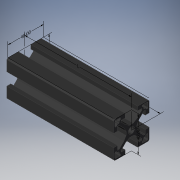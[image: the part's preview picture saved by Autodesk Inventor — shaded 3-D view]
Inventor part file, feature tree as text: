
AUTODESK INVENTOR PART (.ipt)
format: ipt  version: 2019 (Build 230136000, 136)  size: 272,896 bytes
history: native  units: mm
features: other x125, extrude x1, sketch x1
ambient origin geometry x8: Origin, YZ Plane, XZ Plane, XY Plane, X Axis, Y Axis, Z Axis, Center Point
bodies: Solid1 (feature_tree)
feature tree (127):
  other  "Annotations"
  extrude  "Extrusion1"  [1 undecoded]
  other  "CS_ANBAU_HINTEN_LINKS_XY"
  other  "CS_ANBAU_HINTEN_LINKS_YZ"
  other  "CS_ANBAU_HINTEN_LINKS_ZX"
  other  "CS_ANBAU_HINTEN_LINKS_X"
  other  "CS_ANBAU_HINTEN_LINKS_Y"
  other  "CS_ANBAU_HINTEN_LINKS_Z"
  other  "CS_ANBAU_HINTEN_LINKS_Center"
  other  "CS_ANBAU_HINTEN_OBEN_XY"
  other  "CS_ANBAU_HINTEN_OBEN_YZ"
  other  "CS_ANBAU_HINTEN_OBEN_ZX"
  other  "CS_ANBAU_HINTEN_OBEN_X"
  other  "CS_ANBAU_HINTEN_OBEN_Y"
  other  "CS_ANBAU_HINTEN_OBEN_Z"
  other  "CS_ANBAU_HINTEN_OBEN_Center"
  other  "CS_ANBAU_HINTEN_RECHTS_XY"
  other  "CS_ANBAU_HINTEN_RECHTS_YZ"
  other  "CS_ANBAU_HINTEN_RECHTS_ZX"
  other  "CS_ANBAU_HINTEN_RECHTS_X"
  other  "CS_ANBAU_HINTEN_RECHTS_Y"
  other  "CS_ANBAU_HINTEN_RECHTS_Z"
  other  "CS_ANBAU_HINTEN_RECHTS_Center"
  other  "CS_ANBAU_HINTEN_UNTEN_XY"
  other  "CS_ANBAU_HINTEN_UNTEN_YZ"
  other  "CS_ANBAU_HINTEN_UNTEN_ZX"
  other  "CS_ANBAU_HINTEN_UNTEN_X"
  other  "CS_ANBAU_HINTEN_UNTEN_Y"
  other  "CS_ANBAU_HINTEN_UNTEN_Z"
  other  "CS_ANBAU_HINTEN_UNTEN_Center"
  other  "CS_ANBAU_QUER_XY"
  other  "CS_ANBAU_QUER_YZ"
  other  "CS_ANBAU_QUER_ZX"
  other  "CS_ANBAU_QUER_X"
  other  "CS_ANBAU_QUER_Y"
  other  "CS_ANBAU_QUER_Z"
  other  "CS_ANBAU_QUER_Center"
  other  "CS_ANBAU_QUER_1_XY"
  other  "CS_ANBAU_QUER_1_YZ"
  other  "CS_ANBAU_QUER_1_ZX"
  other  "CS_ANBAU_QUER_1_X"
  other  "CS_ANBAU_QUER_1_Y"
  other  "CS_ANBAU_QUER_1_Z"
  other  "CS_ANBAU_QUER_1_Center"
  other  "CS_ANBAU_VORNE_LINKS_XY"
  other  "CS_ANBAU_VORNE_LINKS_YZ"
  other  "CS_ANBAU_VORNE_LINKS_ZX"
  other  "CS_ANBAU_VORNE_LINKS_X"
  other  "CS_ANBAU_VORNE_LINKS_Y"
  other  "CS_ANBAU_VORNE_LINKS_Z"
  other  "CS_ANBAU_VORNE_LINKS_Center"
  other  "CS_ANBAU_VORNE_OBEN_XY"
  other  "CS_ANBAU_VORNE_OBEN_YZ"
  other  "CS_ANBAU_VORNE_OBEN_ZX"
  other  "CS_ANBAU_VORNE_OBEN_X"
  other  "CS_ANBAU_VORNE_OBEN_Y"
  other  "CS_ANBAU_VORNE_OBEN_Z"
  other  "CS_ANBAU_VORNE_OBEN_Center"
  other  "CS_ANBAU_VORNE_RECHTS_XY"
  other  "CS_ANBAU_VORNE_RECHTS_YZ"
  other  "CS_ANBAU_VORNE_RECHTS_ZX"
  other  "CS_ANBAU_VORNE_RECHTS_X"
  other  "CS_ANBAU_VORNE_RECHTS_Y"
  other  "CS_ANBAU_VORNE_RECHTS_Z"
  other  "CS_ANBAU_VORNE_RECHTS_Center"
  other  "CS_ANBAU_VORNE_UNTEN_XY"
  other  "CS_ANBAU_VORNE_UNTEN_YZ"
  other  "CS_ANBAU_VORNE_UNTEN_ZX"
  other  "CS_ANBAU_VORNE_UNTEN_X"
  other  "CS_ANBAU_VORNE_UNTEN_Y"
  other  "CS_ANBAU_VORNE_UNTEN_Z"
  other  "CS_ANBAU_VORNE_UNTEN_Center"
  other  "p1_XY"
  other  "p1_YZ"
  other  "p1_ZX"
  other  "p1_X"
  other  "p1_Y"
  other  "p1_Z"
  other  "p1_Center"
  other  "p2_XY"
  other  "p2_YZ"
  other  "p2_ZX"
  other  "p2_X"
  other  "p2_Y"
  other  "p2_Z"
  other  "p2_Center"
  other  "p3_XY"
  other  "p3_YZ"
  other  "p3_ZX"
  other  "p3_X"
  other  "p3_Y"
  other  "p3_Z"
  other  "p3_Center"
  other  "p4_XY"
  other  "p4_YZ"
  other  "p4_ZX"
  other  "p4_X"
  other  "p4_Y"
  other  "p4_Z"
  other  "p4_Center"
  other  "p5_XY"
  other  "p5_YZ"
  other  "p5_ZX"
  other  "p5_X"
  other  "p5_Y"
  other  "p5_Z"
  other  "p5_Center"
  other  "pm1_XY"
  other  "pm1_YZ"
  other  "pm1_ZX"
  other  "pm1_X"
  other  "pm1_Y"
  other  "pm1_Z"
  other  "pm1_Center"
  other  "pm2_XY"
  other  "pm2_YZ"
  other  "pm2_ZX"
  other  "pm2_X"
  other  "pm2_Y"
  other  "pm2_Z"
  other  "pm2_Center"
  sketch  "Skizze_1"  dims[d0=120.0mm d1=0.0mm d2=0.0mm d3=0.0mm d4=0.0mm d5=0.0mm d6=0.0mm d10=120.0mm d11=120.0mm d7=40.0mm d8=40.0mm d9=40.0mm]
  other  "Linear Dimension 1"
  other  "Linear Dimension 2"
  other  "Linear Dimension 3"
  other  "Linear Dimension 4"
  other  "Linear Dimension 5"
note: 1 required parameter value undecoded (feature->parameter linkage not recoverable at this tier; creation-order binding heuristic only, values carry confidence <= 0.55)
